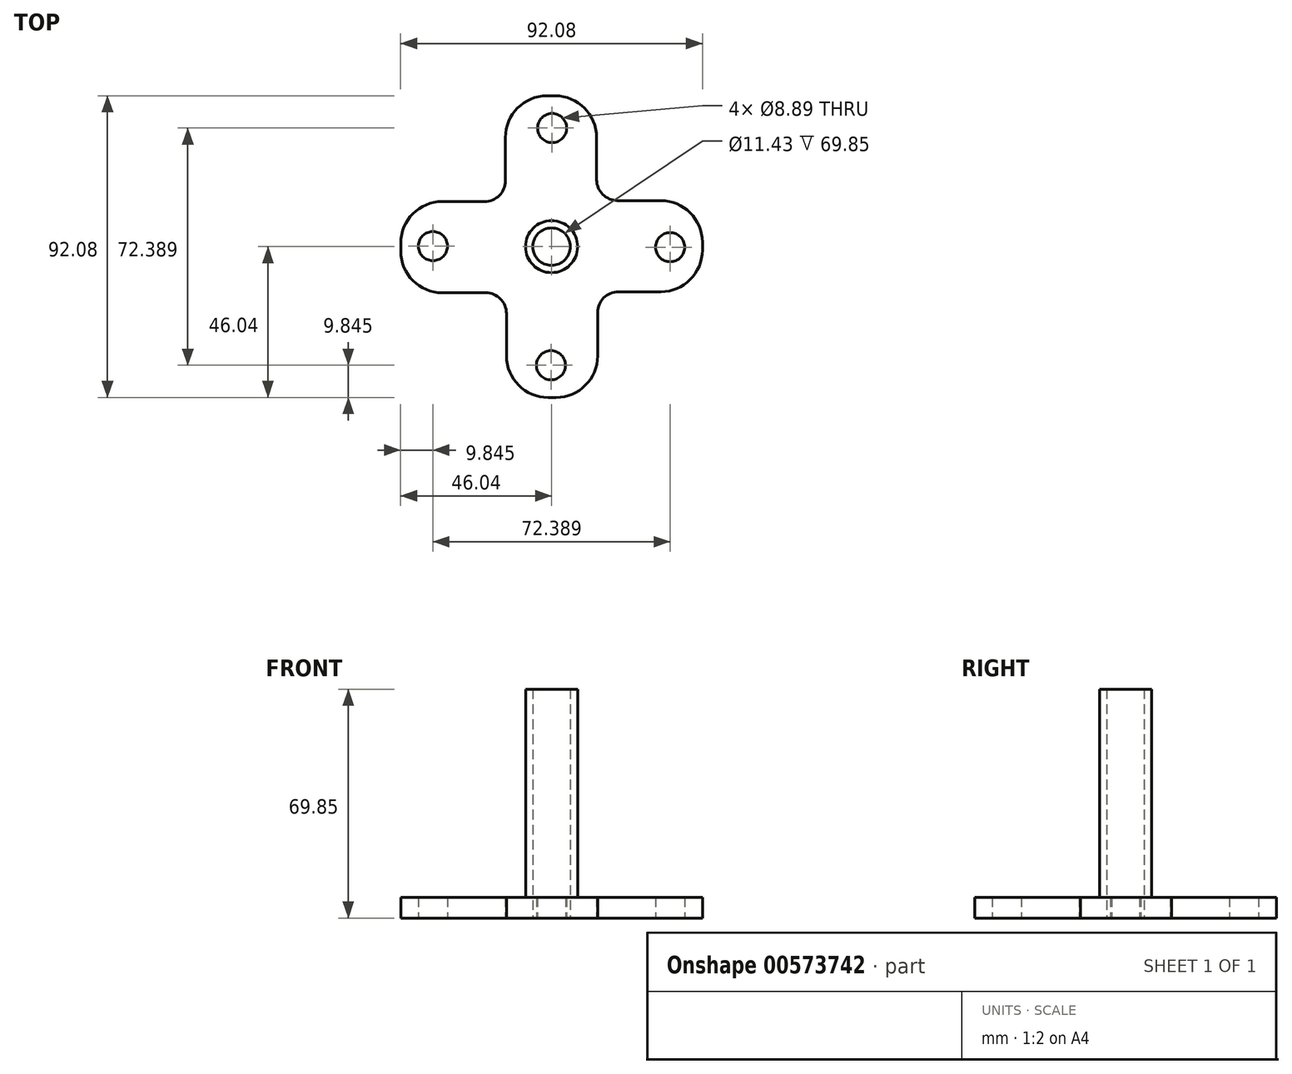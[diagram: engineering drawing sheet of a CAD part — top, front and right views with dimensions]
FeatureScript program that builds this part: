
annotation { "Feature Type Name" : "Feature", "Feature Type Description" : "" }
export const myFeature = defineFeature(function(context is Context, id is Id, definition is map)
    precondition{}
    {
        {
            var Q0;
            Q0=qCreatedBy(makeId("Top.planeOp"),FACE);
            var sketch = newSketch(context, id + "F0", { "sketchPlane" : qUnion([Q0])});
            skCircle(sketch, "E0", {"center": v(0, 0) * mm, "radius": 36.2 * mm, "construction": true});
            skCircle(sketch, "E1", {"center": v(0, 0) * mm, "radius": 7.94 * mm});
            skCircle(sketch, "E2", {"center": v(0, 0) * mm, "radius": 5.72 * mm});
            skCircle(sketch, "E3", {"center": v(36.2, -0.17) * mm, "radius": 4.45 * mm});
            skLineSegment(sketch, "E4.bottom", {"start": v(20.1, 14.07) * mm, "end": v(33.34, 14.07) * mm});
            skLineSegment(sketch, "E4.top", {"start": v(20.42, -13.76) * mm, "end": v(33.34, -13.76) * mm});
            skLineSegment(sketch, "E4.left", {"start": v(0, 14.07) * mm, "end": v(0, -13.76) * mm});
            skLineSegment(sketch, "E4.right", {"start": v(46.04, 1.37) * mm, "end": v(46.04, -1.06) * mm});
            skLineSegment(sketch, "E5.1.0", {"start": v(-1.37, 46.04) * mm, "end": v(1.06, 46.04) * mm});
            skLineSegment(sketch, "E5.1.1", {"start": v(-14.07, 20.1) * mm, "end": v(-14.07, 33.34) * mm});
            skLineSegment(sketch, "E5.1.2", {"start": v(13.76, 20.42) * mm, "end": v(13.76, 33.34) * mm});
            skCircle(sketch, "E5.1.3", {"center": v(0.17, 36.2) * mm, "radius": 4.45 * mm});
            skLineSegment(sketch, "E5.2.0", {"start": v(-46.04, -1.37) * mm, "end": v(-46.04, 1.06) * mm});
            skLineSegment(sketch, "E5.2.1", {"start": v(-20.1, -14.07) * mm, "end": v(-33.34, -14.07) * mm});
            skLineSegment(sketch, "E5.2.2", {"start": v(-20.42, 13.76) * mm, "end": v(-33.34, 13.76) * mm});
            skCircle(sketch, "E5.2.3", {"center": v(-36.2, 0.17) * mm, "radius": 4.45 * mm});
            skLineSegment(sketch, "E5.3.0", {"start": v(1.37, -46.04) * mm, "end": v(-1.06, -46.04) * mm});
            skLineSegment(sketch, "E5.3.1", {"start": v(14.07, -20.1) * mm, "end": v(14.07, -33.34) * mm});
            skLineSegment(sketch, "E5.3.2", {"start": v(-13.76, -20.42) * mm, "end": v(-13.76, -33.34) * mm});
            skCircle(sketch, "E5.3.3", {"center": v(-0.17, -36.2) * mm, "radius": 4.45 * mm});
            skPoint(sketch, "E6.visualSharp", {"position": v(46.04, 14.07) * mm});
            skArc(sketch, "E6.filletArc", {"start": v(46.04, 1.37) * mm, "mid": v(42.32, 10.35) * mm, "end": v(33.34, 14.07) * mm});
            skPoint(sketch, "E7.visualSharp", {"position": v(46.04, -13.76) * mm});
            skArc(sketch, "E7.filletArc", {"start": v(33.34, -13.76) * mm, "mid": v(42.32, -10.04) * mm, "end": v(46.04, -1.06) * mm});
            skPoint(sketch, "E8.visualSharp", {"position": v(14.07, -46.04) * mm});
            skArc(sketch, "E8.filletArc", {"start": v(1.37, -46.04) * mm, "mid": v(10.35, -42.32) * mm, "end": v(14.07, -33.34) * mm});
            skPoint(sketch, "E9.visualSharp", {"position": v(-13.76, -46.04) * mm});
            skArc(sketch, "E9.filletArc", {"start": v(-13.76, -33.34) * mm, "mid": v(-10.04, -42.32) * mm, "end": v(-1.06, -46.04) * mm});
            skPoint(sketch, "E10.visualSharp", {"position": v(-46.04, -14.07) * mm});
            skArc(sketch, "E10.filletArc", {"start": v(-46.04, -1.37) * mm, "mid": v(-42.32, -10.35) * mm, "end": v(-33.34, -14.07) * mm});
            skPoint(sketch, "E11.visualSharp", {"position": v(-46.04, 13.76) * mm});
            skArc(sketch, "E11.filletArc", {"start": v(-33.34, 13.76) * mm, "mid": v(-42.32, 10.04) * mm, "end": v(-46.04, 1.06) * mm});
            skPoint(sketch, "E12.visualSharp", {"position": v(-14.07, 46.04) * mm});
            skArc(sketch, "E12.filletArc", {"start": v(-1.37, 46.04) * mm, "mid": v(-10.35, 42.32) * mm, "end": v(-14.07, 33.34) * mm});
            skPoint(sketch, "E13.visualSharp", {"position": v(13.76, 46.04) * mm});
            skArc(sketch, "E13.filletArc", {"start": v(13.76, 33.34) * mm, "mid": v(10.04, 42.32) * mm, "end": v(1.06, 46.04) * mm});
            skPoint(sketch, "E14.orphan", {"position": v(0, 13.76) * mm});
            skPoint(sketch, "E15.orphan", {"position": v(13.76, 0) * mm});
            skPoint(sketch, "E16.orphan", {"position": v(14.07, 0) * mm});
            skPoint(sketch, "E17.orphan", {"position": v(-13.76, 0) * mm});
            skPoint(sketch, "E18.orphan", {"position": v(-14.07, 0) * mm});
            skPoint(sketch, "E19.visualSharp", {"position": v(-14.07, 13.76) * mm});
            skArc(sketch, "E19.filletArc", {"start": v(-20.42, 13.76) * mm, "mid": v(-15.93, 15.62) * mm, "end": v(-14.07, 20.1) * mm});
            skPoint(sketch, "E20.visualSharp", {"position": v(13.76, 14.07) * mm});
            skArc(sketch, "E20.filletArc", {"start": v(13.76, 20.42) * mm, "mid": v(15.62, 15.93) * mm, "end": v(20.1, 14.07) * mm});
            skPoint(sketch, "E21.orphan", {"position": v(0, -14.07) * mm});
            skPoint(sketch, "E22.visualSharp", {"position": v(-13.76, -14.07) * mm});
            skArc(sketch, "E22.filletArc", {"start": v(-13.76, -20.42) * mm, "mid": v(-15.62, -15.93) * mm, "end": v(-20.1, -14.07) * mm});
            skPoint(sketch, "E23.visualSharp", {"position": v(14.07, -13.76) * mm});
            skArc(sketch, "E23.filletArc", {"start": v(20.42, -13.76) * mm, "mid": v(15.93, -15.62) * mm, "end": v(14.07, -20.1) * mm});
            skSolve(sketch);
        }
        {
            var Q0;
            {var subQ0=sQuery(id+"F0.wireOp",EDGE,"E4.left");var subQ1=sQuery(id+"F0.wireOp",EDGE,"E1");var subQ2=makeQuery(id+"F0.imprint","INTERSECT",VERTEX,{"disambiguationData":[OD(0.0)],"derivedFrom":[subQ1,subQ0]});Q0=makeQuery(id+"F0.imprint","IMPRINT",FACE,{"disambiguationData":[TD([[makeQuery(id+"F0.imprint","IMPRINT",EDGE,{"disambiguationData":[TD([[subQ2,1.0]])],"derivedFrom":subQ1}),1.0]])]});}
            var Q1;
            {var subQ0=sQuery(id+"F0.wireOp",EDGE,"E4.left");var subQ1=sQuery(id+"F0.wireOp",EDGE,"E1");var subQ2=makeQuery(id+"F0.imprint","INTERSECT",VERTEX,{"disambiguationData":[OD(0.0)],"derivedFrom":[subQ1,subQ0]});Q1=makeQuery(id+"F0.imprint","IMPRINT",FACE,{"disambiguationData":[TD([[makeQuery(id+"F0.imprint","IMPRINT",EDGE,{"disambiguationData":[TD([[subQ2,-1.0]])],"derivedFrom":subQ1}),1.0]])]});}
            var Q2;
            Q2=makeQuery(id+"F0.imprint","IMPRINT",FACE,{"disambiguationData":[TD([[makeQuery(id+"F0.imprint","IMPRINT",EDGE,{"derivedFrom":sQuery(id+"F0.wireOp",EDGE,"E3")}),-1.0]])]});
            extrude(context, id + "F1", {"entities" : qUnion([Q0, Q1, Q2]), "depth" : 6.35 * mm, "offsetDistance" : 25.4 * mm});
        }
        {
            var Q0;
            Q0=makeQuery(id+"F1.opExtrude","CAP_FACE",FACE,{"disambiguationData":[OSD([sQuery(id+"F0.wireOp",EDGE,"E2"),sQuery(id+"F0.wireOp",EDGE,"E3"),sQuery(id+"F0.wireOp",EDGE,"E4.bottom"),sQuery(id+"F0.wireOp",EDGE,"E4.top"),sQuery(id+"F0.wireOp",EDGE,"E4.right"),sQuery(id+"F0.wireOp",EDGE,"E5.1.0"),sQuery(id+"F0.wireOp",EDGE,"E5.1.1"),sQuery(id+"F0.wireOp",EDGE,"E5.1.2"),sQuery(id+"F0.wireOp",EDGE,"E5.1.3"),sQuery(id+"F0.wireOp",EDGE,"E5.2.0"),sQuery(id+"F0.wireOp",EDGE,"E5.2.1"),sQuery(id+"F0.wireOp",EDGE,"E5.2.2"),sQuery(id+"F0.wireOp",EDGE,"E5.2.3"),sQuery(id+"F0.wireOp",EDGE,"E5.3.0"),sQuery(id+"F0.wireOp",EDGE,"E5.3.1"),sQuery(id+"F0.wireOp",EDGE,"E5.3.2"),sQuery(id+"F0.wireOp",EDGE,"E5.3.3"),sQuery(id+"F0.wireOp",EDGE,"E6.filletArc"),sQuery(id+"F0.wireOp",EDGE,"E7.filletArc"),sQuery(id+"F0.wireOp",EDGE,"E8.filletArc"),sQuery(id+"F0.wireOp",EDGE,"E9.filletArc"),sQuery(id+"F0.wireOp",EDGE,"E10.filletArc"),sQuery(id+"F0.wireOp",EDGE,"E11.filletArc"),sQuery(id+"F0.wireOp",EDGE,"E12.filletArc"),sQuery(id+"F0.wireOp",EDGE,"E13.filletArc"),sQuery(id+"F0.wireOp",EDGE,"E19.filletArc"),sQuery(id+"F0.wireOp",EDGE,"E20.filletArc"),sQuery(id+"F0.wireOp",EDGE,"E22.filletArc"),sQuery(id+"F0.wireOp",EDGE,"E23.filletArc")])],"isStart":false});
            var sketch = newSketch(context, id + "F2", { "sketchPlane" : qUnion([Q0])});
            skCircle(sketch, "E24", {"center": v(0, 0) * mm, "radius": 7.94 * mm});
            skSolve(sketch);
        }
        {
            var Q0;
            Q0=makeQuery(id+"F2.imprint","IMPRINT",FACE,{"disambiguationData":[TD([[makeQuery(id+"F2.imprint","IMPRINT",EDGE,{"derivedFrom":sQuery(id+"F2.wireOp",EDGE,"E24")}),1.0]])]});
            extrude(context, id + "F3", {"entities" : qUnion([Q0]), "operationType" : NewBodyOperationType.ADD, "depth" : 63.5 * mm, "offsetDistance" : 25.4 * mm});
        }
    });
